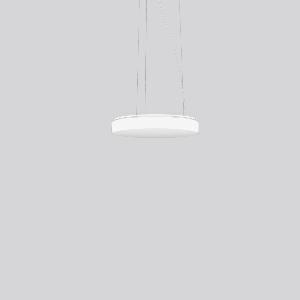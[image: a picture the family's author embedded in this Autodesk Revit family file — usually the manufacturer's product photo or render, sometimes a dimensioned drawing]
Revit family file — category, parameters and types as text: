
# Revit family: flat_polymero_kreis_slim_312089_002_1_76_40e9
name_source: partatom
category: Lighting Fixtures
units: mm (PartAtom-declared; Revit-internal decimal feet)

## family parameters
Cut with Voids When Loaded = No
Host = Face
Light Source = No
Part Type = Normal
Room Calculation Point = No
Round Connector Dimension = Use Diameter
Shared = No

## types (1)
- FLAT POLYMERO KREIS SLIM (1 x LED Modul 830, 1900 lm, 3000)
    Apparent Load = 19 VA
    CIE Flux Codes = 42 73 92 85 100
    Color Rendering = 80
    Color Temperature = 3000
    Default Elevation = 1800 mm
    Description = Series: FLAT POLYMERO KREIS SLIM
Decorative round LED pendant luminaire. Base and canopy: metal, powder-coated, white. Canopy Ø 205 mm, h 35 mm. Diffuser made of non-yellowing plastic (PMMA), opal. Diffuser fastening: patented push system. Homogeneous and smooth light distribution. Suitable for pendant. 3-point steel cable suspension, steplessly adjustable. Special lengths available on request. TouchDim sensor capable. Light and/or presence sensors can be integrated. 
Colour: white
Diameter: 360 mm
Height: 61 mm
Suspension length: 200-1300 mm
Lamp: LED
Socket: without socket
Colour temperature: 3000K
Colour rendering index (CRI): 83
System power: 19 W
Rated luminous flux: 1900 lm
Luminous efficiency: 100 lm/W
Control gear: AC power, DALI dimmable
Protection class: I
Type of protection: IP 40
    Height = 61 mm
    Lamp = 1 x LED Modul 830
    Lamp Light Flux = 1900 lm
    Lamp count = 1
    Length = 360 mm
    Lifetime = 50000 h
    Luminous efficacy = 100 lm/W
    Manufacturer = RZB
    ModVariant = No
    Model = 312089.002.1.76
    Mounting Place = Ceiling
    Mounting Type = Pendant
    Number of Poles = 1
    OnlyDefault = Yes
    Power Factor = 1
    Product Name = FLAT POLYMERO KREIS SLIM
    Product group = Pendant luminaires
    ProductGroupID = 902
    Protection Class = Protection class I
    Protection Degree = IP 40
    RLX_Detail_Level = 1
    RLX_Emergency_Light_Flux = 0 lm
    RLX_Emergency_Type = 0
    RLX_Emergency_Type_DB = No
    RlxData = <blob elided: 56349 chars, md5=b58ff269>
    Socket = socket
    Standby Power = 0 W
    System Light Flux = 1900 lm
    System Power = 19 W
    Type Comments = Product without accessories
    Type Image = 312089.002.jpg
    URL = http://relux.com
    VarID = ---
    Voltage = 230 V
    Voltage Range = 220-240 V
    Weight = 0.00 kg
    Width = 0 mm  [stored 0 ft]

note: [stored X ft] marks values corroborated as IEEE doubles in the binary element streams (Revit-internal decimal feet)

## geometry (parser evidence)
native form markers: Blend x4, Sweep x13
no freeform markers — native parametric forms only
